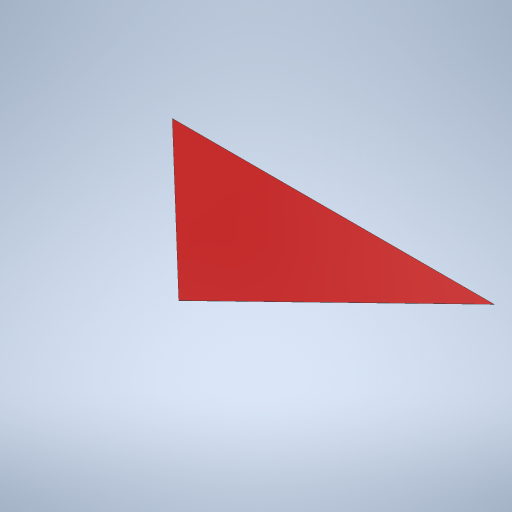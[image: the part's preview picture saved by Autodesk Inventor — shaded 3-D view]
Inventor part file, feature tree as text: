
AUTODESK INVENTOR PART (.ipt)
format: ipt  version: 2023 (Build 270158000, 158)  size: 232,960 bytes
history: native  units: in
note: dims shown in document units (in); Inventor stores cm internally (conversion verified against a paired STEP export)
features: extrude x1, sketch x1
ambient origin geometry x8: Origin, YZ Plane, XZ Plane, XY Plane, X Axis, Y Axis, Z Axis, Center Point
bodies: Solid1 (feature_tree)
feature tree (2):
  extrude  "Extrusion1"  Depth=0.4724in
  sketch  "Sketch1"  dims[d0=0.9843in d1=0.4724in d2=0.4921in d3=0.0004in d4=0.0in]
